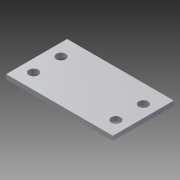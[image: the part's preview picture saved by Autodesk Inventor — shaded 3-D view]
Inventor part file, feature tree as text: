
AUTODESK INVENTOR PART (.ipt)
format: ipt  version: 2015 (Build 190159000, 159)  size: 105,472 bytes
history: native  units: mm
features: sketch x2, other x1, extrude x1, hole x1
ambient origin geometry x8: Origin, YZ Plane, XZ Plane, XY Plane, X Axis, Y Axis, Z Axis, Center Point
bodies: Body1 (feature_tree)
feature tree (5):
  other  "ソリッド1"
  extrude  "押し出し1"  Depth=35.0mm
  hole  "穴1"  [1 undecoded]
  sketch  "スケッチ1"
  sketch  "スケッチ2"
note: 1 required parameter value undecoded (feature->parameter linkage not recoverable at this tier; creation-order binding heuristic only, values carry confidence <= 0.55)
